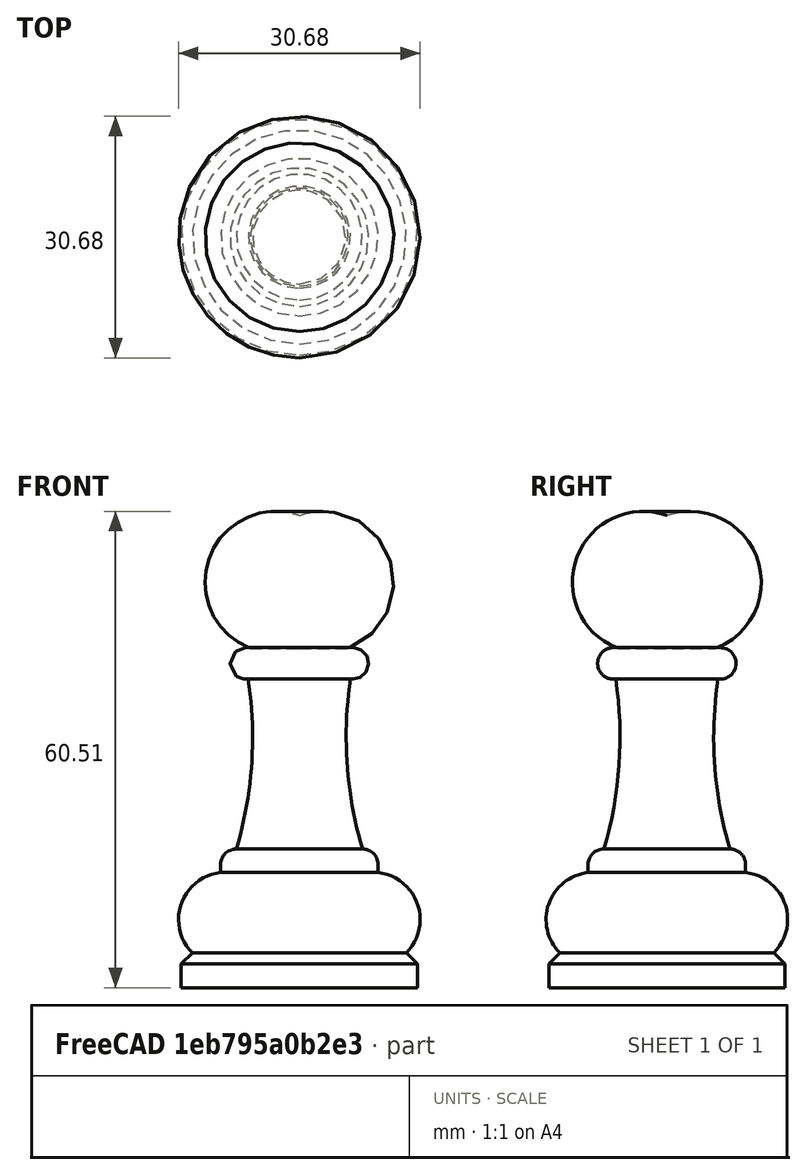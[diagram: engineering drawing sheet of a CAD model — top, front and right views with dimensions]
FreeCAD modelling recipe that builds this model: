
FCSTD DOCUMENT  (FreeCAD 1.1R44227 +322 (Git))
Label: Peon
License: All rights reserved
LicenseURL: https://en.wikipedia.org/wiki/All_rights_reserved
objects: App::Point×1, Sketcher::SketchObject×1, PartDesign::Revolution×1, PartDesign::Body×1
note: 6 computed .brp shape members not serialized (recipe doc carries the construction recipe); baked Part::Feature solids carry a one-line shape summary decoded from their .brp

FEATURE [App::Point] Origin001  label="Origen de coordenadas"
  Role = Origin
FEATURE [Sketcher::SketchObject] Sketch
  ArcFitTolerance = 1e-06
  AttachmentSupport = -> [Origin]
  ExternalTypes = [0]
  FullyConstrained = true
  MakeInternals = false
  MapMode = 5
  Placement = pos=(0,0,0) rot=(0.57735,0.57735,0.57735;2.0944rad)
  sketch-geometry (10):
    g0: LineSegment StartX=0 StartY=0 StartZ=0 EndX=1.96077e-05 EndY=60 EndZ=0
    g1: LineSegment StartX=0 StartY=0 StartZ=0 EndX=-15 EndY=0 EndZ=0
    g2: LineSegment StartX=-15 StartY=0 StartZ=0 EndX=-15 EndY=3 EndZ=0
    g3: LineSegment StartX=-15 StartY=3 StartZ=0 EndX=-13.5858 EndY=4.41421 EndZ=0
    g4: ArcOfCircle CenterX=-9.34314 CenterY=8.65685 CenterZ=0 NormalX=0 NormalY=0 NormalZ=1 AngleXU=0 Radius=6 StartAngle=1.68049 EndAngle=3.92699
    g5: LineSegment StartX=-10 StartY=14.6208 StartZ=0 EndX=-9.99999 EndY=15.6208 EndZ=0
    g6: ArcOfCircle CenterX=-7.99999 CenterY=15.6208 CenterZ=0 NormalX=0 NormalY=0 NormalZ=1 AngleXU=0 Radius=2 StartAngle=1.5708 EndAngle=3.14159
    g7: ArcOfCircle CenterX=-55.947 CenterY=31.8013 CenterZ=0 NormalX=0 NormalY=0 NormalZ=1 AngleXU=0 Radius=50 StartAngle=5.99563 EndAngle=6.43205
    g8: ArcOfCircle CenterX=-6.79662 CenterY=41.1949 CenterZ=0 NormalX=0 NormalY=0 NormalZ=1 AngleXU=0 Radius=2 StartAngle=1.16112 EndAngle=4.86125
    g9: ArcOfCircle CenterX=-2.99998 CenterY=51.5147 CenterZ=0 NormalX=0 NormalY=0 NormalZ=1 AngleXU=0 Radius=9 StartAngle=1.23096 EndAngle=4.37255
  constraints (31):
    c: Distance(g0) = 60
    c: Angle(g-1,g0) = 1.5708
    c: Coincident(g0,g-1)
    c: Distance(g1) = 15
    c: Horizontal(g1)
    c: Coincident(g1,g0)
    c: Distance(g2) = 3
    c: Angle(g-1,g2) = 1.5708
    c: Coincident(g2,g1)
    c: Distance(g3) = 2
    c: Angle(g-1,g3) = 0.785398
    c: Coincident(g3,g2)
    c: Perpendicular(g3,g4) = 4.71239
    c: Radius(g4) = 6
    c: Distance(g4,g0) = 10
    c: Distance(g5) = 1
    c: Angle(g-1,g5) = 1.5708
    c: Coincident(g5,g4)
    c: Tangent(g5,g6) = 1.5708
    c: Radius(g6) = 2
    c: DistanceX(g6,g-1) = 8
    c: Coincident(g7,g6)
    c: Radius(g7) = 50
    c: Distance(g7,g0) = 6.5
    c: Perpendicular(g7,g8) = 4.71239
    c: Radius(g8) = 2
    c: Distance(g8,g0) = 6
    c: Coincident(g9,g8)
    c: Coincident(g9,g0)
    c: Radius(g9) = 9
    c: Angle(g9) = 3.14159
FEATURE [PartDesign::Revolution] Revolution
  Angle = 360
  Angle2 = 0
  Axis = (0,3.26795e-07,1)
  Base = (0,0,0)
  FuseOrder = 0
  Profile = -> Sketch
  ReferenceAxis = -> Sketch [Edge1]
  Refine = true
  Suppressed = false
  Type = 0
FEATURE [PartDesign::Body] Body
  AllowCompound = true
  Group = -> [Sketch,Revolution]
  Origin = -> Origin
  Tip = -> Revolution
